# Revit family: Sanitary_Wash-Basins_HIMACS_HIMACS-Bowl-CB-320
name_source: partatom
category: Plumbing Fixtures
revit_build: Autodesk Revit 2018 (Build: 20190510_1515(x64)
units: mm (PartAtom-declared; Revit-internal decimal feet)

## family parameters
Cut with Voids When Loaded = No
Host = Face
OmniClass Number = 23.31.13.00
OmniClass Title = Sinks
Part Type = Normal
Room Calculation Point = No
Round Connector Dimension = Use Diameter
Shared = No

## types (2) — shared parameters
BIMobject category = Wash Basins
Default Elevation = 1219 mm
Description = HIMACS Bowls offer superb ease of cleaning and a warm and pleasant feel, making them the ideal solution for creating the bathroom of your dreams. They are manufactured using a casting process and ideally suited for both flush mounting and installation into a bathroom vanity top.
Design country = Spain
Diameter = 45 mm  [stored 0.147638 ft]
Edition number = 1
IFC Classification = Furnishing Element
Main material = HIMACS - Ceramic - Alpine White
Manufacturer = HIMACS
Manufacturer country = Spain
Manufacturer name = HIMACS
Material main = Solid surface
Material secondary = Natural Acrylic Stone
Model = HIMACS Bowl CB 320
NBS Reference Code = 35-65-70-94
NBS Reference Description = Wash Basin Systems
Product Guid = 2064bb9b-a252-4467-a88b-9ad55c9e957c
Product SKU = CB320
Product certification = http://himacs.eu
Product data url = https://bimobject.com
Product family = Sinks, Baby Baths & Bowls
Product group = Bowls
Product name = HIMACS Bowl CB 320
QR code = https://bimobject.com
UNSPSC Code = 301815
URL = https://himacs.eu
Uniclass 1.4 Code = L7212
Uniclass 1.4 Description = Washbasins
Uniclass 2.0 Code = SS-35-65-70-94
Uniclass 2.0 Description = Wash Basin Systems
Weight Net (Kg) = 3,75

## per-type parameters (varying)
| type | Overflow - (With) | Overflow - (Without) |
| HIMACS Bowl CB 320 with Overflow | Yes | No |
| HIMACS Bowl CB 320 without Overflow | No | Yes |

note: [stored X ft] marks values corroborated as IEEE doubles in the binary element streams (Revit-internal decimal feet)

## geometry (parser evidence)
native form markers: Sweep x4
no freeform markers — native parametric forms only
